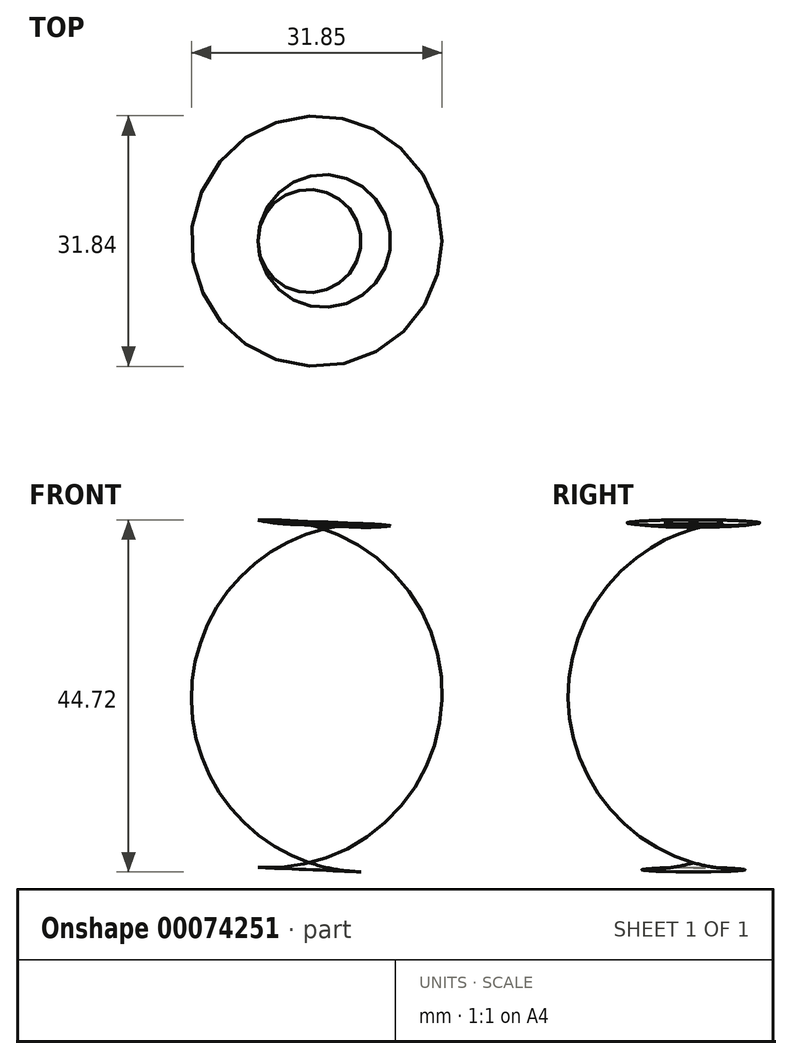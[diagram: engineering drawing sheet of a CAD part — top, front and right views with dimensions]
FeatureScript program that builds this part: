
annotation { "Feature Type Name" : "Feature", "Feature Type Description" : "" }
export const myFeature = defineFeature(function(context is Context, id is Id, definition is map)
    precondition{}
    {
        {
            var Q0;
            Q0=qCreatedBy(makeId("Front.planeOp"),FACE);
            var sketch = newSketch(context, id + "F0", { "sketchPlane" : qUnion([Q0])});
            skArc(sketch, "E0", {"start": v(-9.2, 72.67) * mm, "mid": v(-39.82, 52.67) * mm, "end": v(-19.82, 22.06) * mm});
            skArc(sketch, "E1", {"start": v(-19.82, 22.06) * mm, "mid": v(-40.6, 0) * mm, "end": v(-19.82, -22.06) * mm});
            skArc(sketch, "E2", {"start": v(-19.82, -22.06) * mm, "mid": v(-96.48, -98.72) * mm, "end": v(-19.82, -175.38) * mm});
            skLineSegment(sketch, "E3", {"start": v(-19.82, -175.38) * mm, "end": v(-9.2, 72.67) * mm});
            skSolve(sketch);
        }
        {
            var Q0;
            Q0=makeQuery(id+"F0.imprint","IMPRINT",FACE,{"disambiguationData":[TD([[makeQuery(id+"F0.imprint","IMPRINT",EDGE,{"derivedFrom":sQuery(id+"F0.wireOp",EDGE,"E0")}),1.0]])]});
            var Q1;
            Q1=sQuery(id+"F0.wireOp",EDGE,"E3");
            revolve(context, id + "F1", {"entities" : qUnion([Q0]), "axis" : qUnion([Q1]), "revolveType" : RevolveType.FULL});
        }
    });
